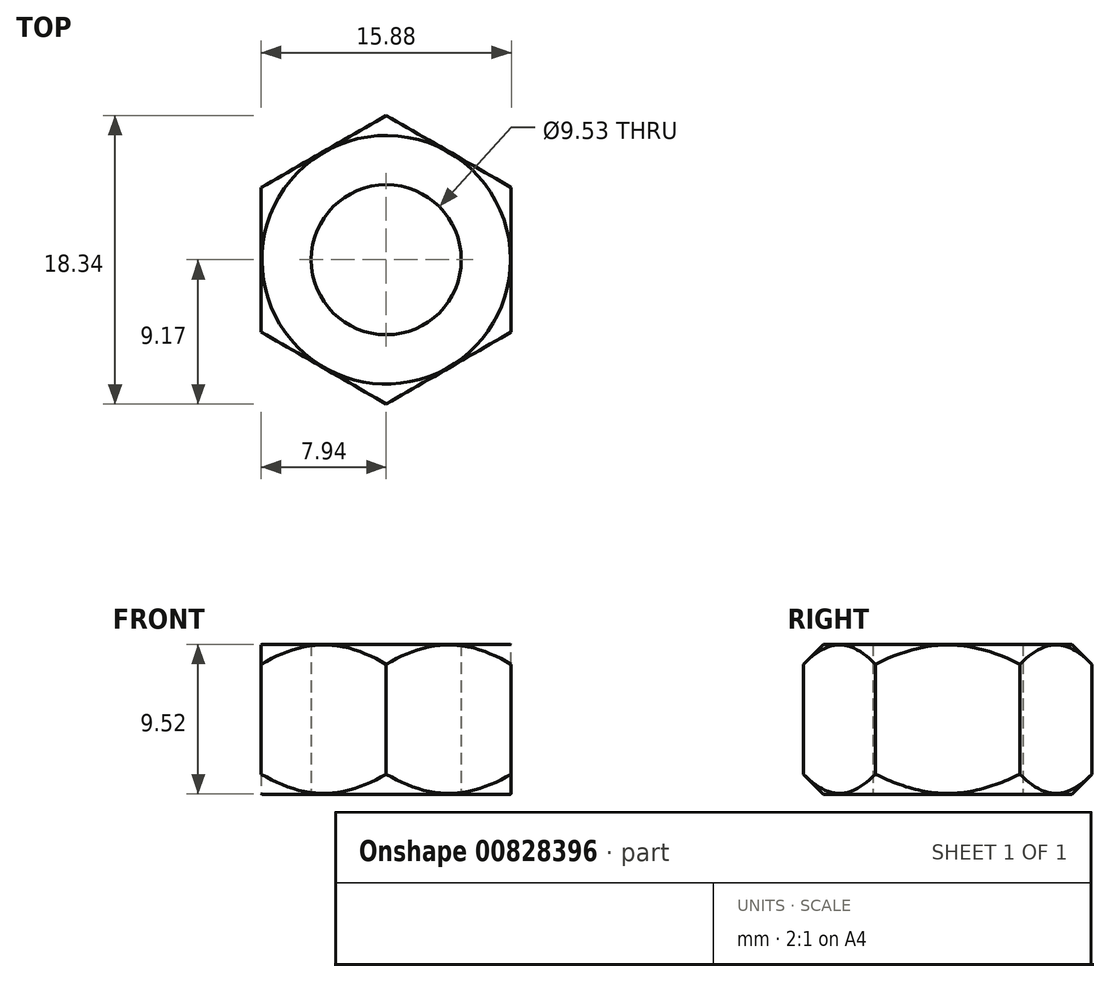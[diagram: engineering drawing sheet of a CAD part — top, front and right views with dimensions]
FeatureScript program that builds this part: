
annotation { "Feature Type Name" : "Feature", "Feature Type Description" : "" }
export const myFeature = defineFeature(function(context is Context, id is Id, definition is map)
    precondition{}
    {
        {
            var Q0;
            Q0=qCreatedBy(makeId("Top.planeOp"),FACE);
            var sketch = newSketch(context, id + "F0", { "sketchPlane" : qUnion([Q0])});
            skCircle(sketch, "E0", {"center": v(0, 0) * mm, "radius": 4.76 * mm});
            skCircle(sketch, "E1.cCircle", {"center": v(0, 0) * mm, "radius": 7.94 * mm, "construction": true});
            skLineSegment(sketch, "E1.0", {"start": v(0, 9.17) * mm, "end": v(7.94, 4.58) * mm});
            skLineSegment(sketch, "E1.1", {"start": v(7.94, 4.58) * mm, "end": v(7.94, -4.58) * mm});
            skLineSegment(sketch, "E1.2", {"start": v(7.94, -4.58) * mm, "end": v(0, -9.17) * mm});
            skLineSegment(sketch, "E1.3", {"start": v(0, -9.17) * mm, "end": v(-7.94, -4.58) * mm});
            skLineSegment(sketch, "E1.4", {"start": v(-7.94, -4.58) * mm, "end": v(-7.94, 4.58) * mm});
            skLineSegment(sketch, "E1.5", {"start": v(-7.94, 4.58) * mm, "end": v(0, 9.17) * mm});
            skPoint(sketch, "E1.0.midPoint", {"position": v(3.97, 6.87) * mm});
            skSolve(sketch);
        }
        {
            var Q0;
            Q0 = qSketchRegion(id + "F0", true);
            extrude(context, id + "F1", {"entities" : qUnion([Q0]), "endBound" : BoundingType.SYMMETRIC, "depth" : 9.52 * mm, "offsetDistance" : 25.4 * mm});
        }
        {
            var Q0;
            Q0=qCreatedBy(makeId("Right.planeOp"),FACE);
            var sketch = newSketch(context, id + "F2", { "sketchPlane" : qUnion([Q0])});
            skLineSegment(sketch, "E2", {"start": v(9.17, 3.5) * mm, "end": v(7.3, 5.35) * mm});
            skLineSegment(sketch, "E3", {"start": v(7.3, 5.35) * mm, "end": v(12.98, 5.35) * mm});
            skLineSegment(sketch, "E4", {"start": v(12.98, 5.35) * mm, "end": v(12.98, -5.3) * mm});
            skLineSegment(sketch, "E5", {"start": v(12.98, -5.3) * mm, "end": v(7.36, -5.3) * mm});
            skLineSegment(sketch, "E6", {"start": v(7.36, -5.3) * mm, "end": v(9.17, -3.5) * mm});
            skLineSegment(sketch, "E7", {"start": v(9.17, -3.5) * mm, "end": v(9.17, 3.5) * mm});
            skLineSegment(sketch, "E8", {"start": v(0, 0) * mm, "end": v(0, 8.32) * mm, "construction": true});
            skSolve(sketch);
        }
        {
            var Q0;
            Q0 = qSketchRegion(id + "F2", true);
            var Q1;
            Q1=sQuery(id+"F2.wireOp",EDGE,"E8");
            revolve(context, id + "F3", {"operationType" : NewBodyOperationType.REMOVE, "surfaceOperationType" : NewSurfaceOperationType.NEW, "entities" : qUnion([Q0]), "axis" : qUnion([Q1]), "revolveType" : RevolveType.FULL, "oppositeDirection" : true});
        }
    });
